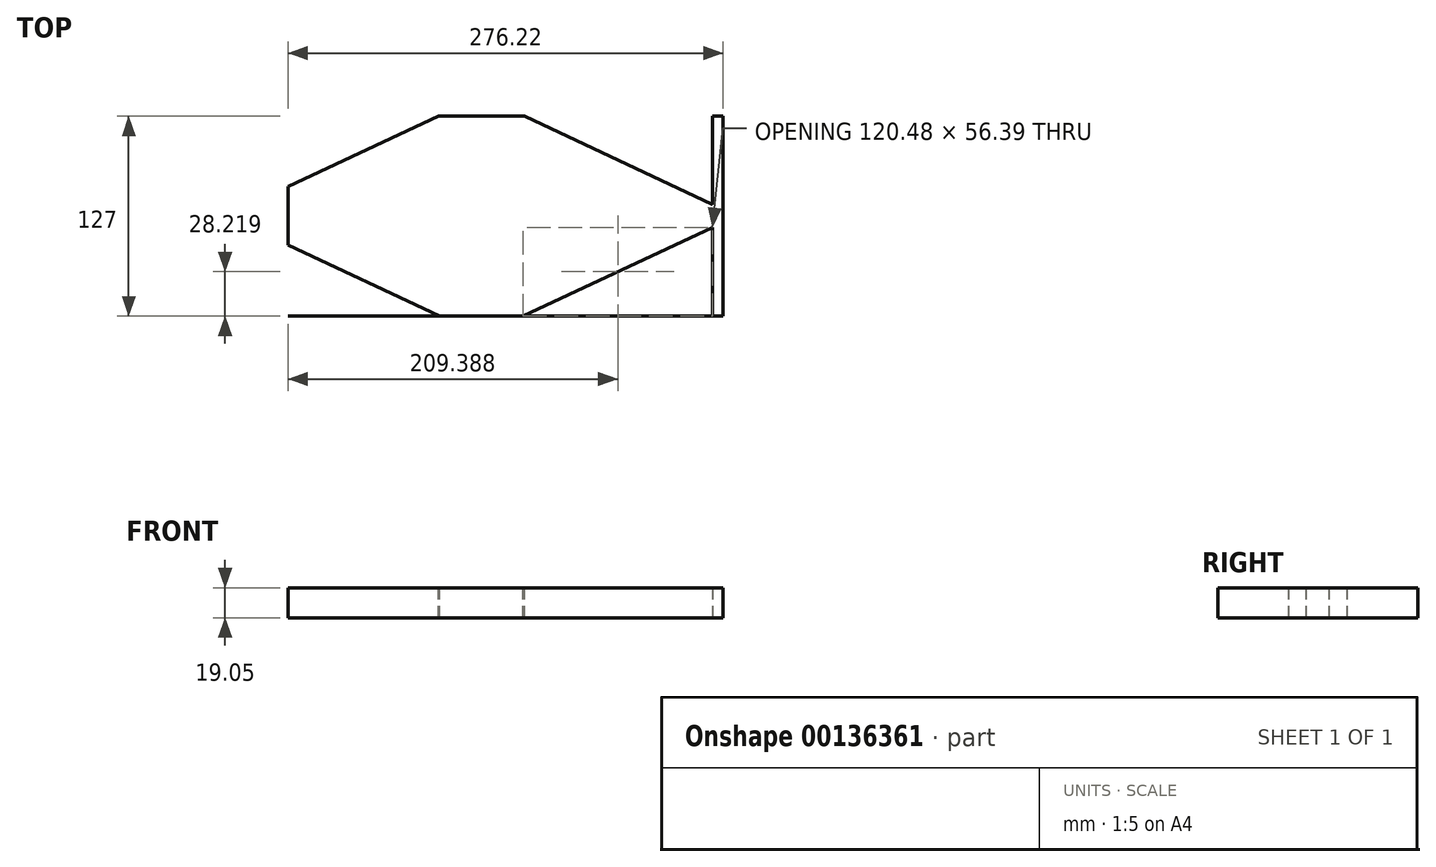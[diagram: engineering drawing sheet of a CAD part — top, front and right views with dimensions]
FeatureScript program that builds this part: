
annotation { "Feature Type Name" : "Feature", "Feature Type Description" : "" }
export const myFeature = defineFeature(function(context is Context, id is Id, definition is map)
    precondition{}
    {
        {
            var Q0;
            Q0=qCreatedBy(makeId("Top.planeOp"),FACE);
            var sketch = newSketch(context, id + "F0", { "sketchPlane" : qUnion([Q0])});
            skLineSegment(sketch, "E0.bottom", {"start": v(-122.72, 61.13) * mm, "end": v(153.5, 61.13) * mm});
            skLineSegment(sketch, "E0.top", {"start": v(-122.72, -65.87) * mm, "end": v(153.5, -65.87) * mm});
            skLineSegment(sketch, "E0.left", {"start": v(-122.72, 61.13) * mm, "end": v(-122.72, -65.87) * mm});
            skLineSegment(sketch, "E0.right", {"start": v(153.5, 61.13) * mm, "end": v(153.5, -65.87) * mm});
            skLineSegment(sketch, "E1", {"start": v(-122.72, 0) * mm, "end": v(-97.32, 0) * mm, "construction": true});
            skPoint(sketch, "E1.startSnap0", {"position": v(-122.72, -2.37) * mm});
            skLineSegment(sketch, "E2", {"start": v(153.5, 0) * mm, "end": v(128.1, 0) * mm, "construction": true});
            skLineSegment(sketch, "E3", {"start": v(-97.32, 0) * mm, "end": v(-97.32, -100.17) * mm, "construction": true});
            skLineSegment(sketch, "E4", {"start": v(-97.32, -100.17) * mm, "end": v(128.1, -100.17) * mm, "construction": true});
            skLineSegment(sketch, "E5", {"start": v(128.1, -100.17) * mm, "end": v(128.1, 0) * mm, "construction": true});
            skSolve(sketch);
        }
        {
            var Q0;
            Q0 = qSketchRegion(id + "F0", true);
            extrude(context, id + "F1", {"entities" : qUnion([Q0]), "depth" : 19.05 * mm});
        }
        {
            var Q0;
            Q0=makeQuery(id+"F1.opExtrude","CAP_FACE",FACE,{"disambiguationData":[OSD([sQuery(id+"F0.wireOp",EDGE,"E0.bottom"),sQuery(id+"F0.wireOp",EDGE,"E0.top"),sQuery(id+"F0.wireOp",EDGE,"E0.left"),sQuery(id+"F0.wireOp",EDGE,"E0.right")])],"isStart":false});
            var sketch = newSketch(context, id + "F2", { "sketchPlane" : qUnion([Q0])});
            skPoint(sketch, "E6.first.point", {"position": v(-24.71, 27.36) * mm});
            skPoint(sketch, "E6.second.point", {"position": v(22.8, -19.4) * mm});
            skPoint(sketch, "E6.third.point", {"position": v(25.07, 24.34) * mm});
            skPoint(sketch, "E7.first.point", {"position": v(-28.48, 36.32) * mm});
            skPoint(sketch, "E7.second.point", {"position": v(27.52, -32.7) * mm});
            skPoint(sketch, "E7.third.point", {"position": v(37.94, 25.9) * mm});
            skLineSegment(sketch, "E8", {"start": v(-173.66, 0) * mm, "end": v(-173.66, 5.4) * mm, "construction": true});
            skLineSegment(sketch, "E9", {"start": v(-173.66, 5.4) * mm, "end": v(-173.66, 0) * mm, "construction": true});
            skLineSegment(sketch, "E10", {"start": v(-126.98, -20) * mm, "end": v(-42.87, -20) * mm});
            skPoint(sketch, "E11.orphan", {"position": v(171.14, 5.4) * mm});
            skLineSegment(sketch, "E12", {"start": v(-124.98, 5.4) * mm, "end": v(-44.12, 5.4) * mm});
            skLineSegment(sketch, "E13.trimOffspring", {"start": v(44.57, 5.4) * mm, "end": v(106.48, 5.4) * mm});
            skLineSegment(sketch, "E14.trimOffspring", {"start": v(42.87, -20) * mm, "end": v(112.65, -20) * mm});
            skPoint(sketch, "E15.orphan", {"position": v(0, 61.13) * mm});
            skPoint(sketch, "E16.orphan", {"position": v(15.4, -65.87) * mm});
            skPoint(sketch, "E17.start.orphan", {"position": v(-122.72, 0) * mm});
            skArc(sketch, "E18", {"start": v(-126.98, -20) * mm, "mid": v(-120.96, -21) * mm, "end": v(-114.95, -20) * mm});
            skPoint(sketch, "E18.centerSnap0", {"position": v(-122.72, -2.37) * mm});
            skPoint(sketch, "E19.orphan", {"position": v(104.71, -0.76) * mm});
            skPoint(sketch, "E20.start.orphan", {"position": v(153.5, -2.37) * mm});
            skPoint(sketch, "E21.center.orphan", {"position": v(104.71, -2.37) * mm});
            skPoint(sketch, "E21.end.orphan", {"position": v(104.71, -21.93) * mm});
            skArc(sketch, "E22", {"start": v(-116.95, 5.4) * mm, "mid": v(-133.7, -2.67) * mm, "end": v(-126.98, -20) * mm});
            skArc(sketch, "E23", {"start": v(112.65, -20) * mm, "mid": v(118.67, -4.18) * mm, "end": v(104.71, 5.4) * mm});
            skPoint(sketch, "E24.orphan", {"position": v(171.14, -20) * mm});
            skCircle(sketch, "E25", {"center": v(0, -8.26) * mm, "radius": 33.34 * mm});
            skCircle(sketch, "E26", {"center": v(0, -8.26) * mm, "radius": 44.45 * mm});
            skSolve(sketch);
        }
        {
            var Q0;
            {var subQ11=sQuery(id+"F2.wireOp",EDGE,"E18");Q0=makeQuery(id+"F2.imprint","IMPRINT",FACE,{"disambiguationData":[TD([[makeQuery(id+"F2.imprint","IMPRINT",EDGE,{"derivedFrom":subQ11}),-1.0]])]});}
            var sketch = newSketch(context, id + "F3", { "sketchPlane" : qUnion([Q0])});
            skLineSegment(sketch, "E27", {"start": v(-146.9, 61.53) * mm, "end": v(-26.43, 61.53) * mm});
            skLineSegment(sketch, "E28", {"start": v(-26.43, 61.53) * mm, "end": v(-146.9, 5.15) * mm});
            skLineSegment(sketch, "E29", {"start": v(-146.9, 5.15) * mm, "end": v(-146.9, 61.53) * mm});
            skLineSegment(sketch, "E30", {"start": v(-146.9, -2.16) * mm, "end": v(130.15, -2.16) * mm, "construction": true});
            skLineSegment(sketch, "E31.MirrorCS", {"start": v(-26.43, -65.84) * mm, "end": v(-146.9, -9.46) * mm});
            skLineSegment(sketch, "E32", {"start": v(0, 0) * mm, "end": v(0, -65.84) * mm, "construction": true});
            skLineSegment(sketch, "E33", {"start": v(0, -65.84) * mm, "end": v(0, 61.53) * mm, "construction": true});
            skLineSegment(sketch, "E34", {"start": v(-146.9, -9.46) * mm, "end": v(-146.9, -65.84) * mm});
            skLineSegment(sketch, "E35", {"start": v(-146.9, -65.84) * mm, "end": v(-26.43, -65.84) * mm});
            skLineSegment(sketch, "E36.MirrorCS", {"start": v(26.43, 61.53) * mm, "end": v(146.9, 5.15) * mm});
            skLineSegment(sketch, "E37.MirrorCS", {"start": v(146.9, 61.53) * mm, "end": v(26.43, 61.53) * mm});
            skLineSegment(sketch, "E38.MirrorCS", {"start": v(146.9, 5.15) * mm, "end": v(146.9, 61.53) * mm});
            skLineSegment(sketch, "E39.MirrorCS", {"start": v(146.9, -65.84) * mm, "end": v(26.43, -65.84) * mm});
            skLineSegment(sketch, "E40.MirrorCS", {"start": v(26.43, -65.84) * mm, "end": v(146.9, -9.46) * mm});
            skLineSegment(sketch, "E41.MirrorCS", {"start": v(146.9, -9.46) * mm, "end": v(146.9, -65.84) * mm});
            skSolve(sketch);
        }
        {
            var Q0;
            Q0 = qSketchRegion(id + "F3", true);
            extrude(context, id + "F4", {"entities" : qUnion([Q0]), "operationType" : NewBodyOperationType.REMOVE, "oppositeDirection" : true, "depth" : 25.4 * mm});
        }
    });
